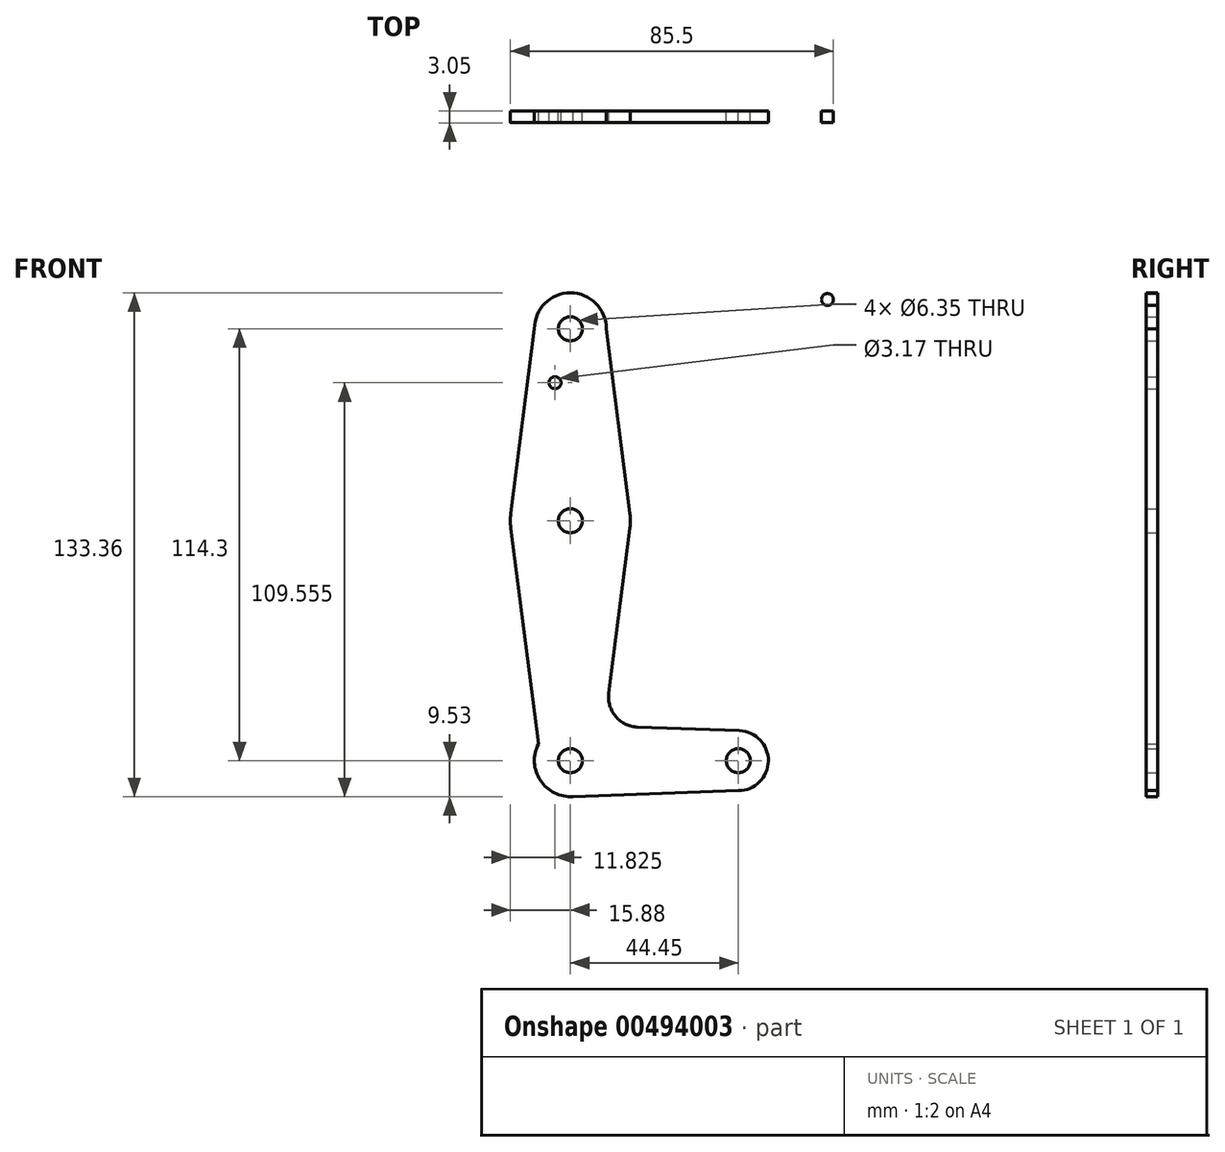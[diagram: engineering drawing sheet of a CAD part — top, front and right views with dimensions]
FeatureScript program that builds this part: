
annotation { "Feature Type Name" : "Feature", "Feature Type Description" : "" }
export const myFeature = defineFeature(function(context is Context, id is Id, definition is map)
    precondition{}
    {
        {
            var Q0;
            Q0=qCreatedBy(makeId("Front.planeOp"),FACE);
            var sketch = newSketch(context, id + "F0", { "sketchPlane" : qUnion([Q0])});
            skLineSegment(sketch, "E0", {"start": v(0, 0) * mm, "end": v(0, 114.3) * mm, "construction": true});
            skLineSegment(sketch, "E1", {"start": v(0, 0) * mm, "end": v(44.45, 0) * mm, "construction": true});
            skCircle(sketch, "E2", {"center": v(0, 114.3) * mm, "radius": 9.53 * mm});
            skCircle(sketch, "E3", {"center": v(0, 0) * mm, "radius": 9.53 * mm});
            skCircle(sketch, "E4", {"center": v(0, 63.5) * mm, "radius": 15.88 * mm});
            skLineSegment(sketch, "E5", {"start": v(9.53, 114.3) * mm, "end": v(15.75, 65.5) * mm});
            skLineSegment(sketch, "E6", {"start": v(-9.53, 114.3) * mm, "end": v(-15.75, 65.5) * mm});
            skLineSegment(sketch, "E7", {"start": v(15.75, 61.5) * mm, "end": v(10.18, 17.84) * mm});
            skLineSegment(sketch, "E8", {"start": v(-15.75, 61.5) * mm, "end": v(-8.46, 4.37) * mm});
            skCircle(sketch, "E9", {"center": v(44.45, 0) * mm, "radius": 7.94 * mm});
            skLineSegment(sketch, "E10", {"start": v(17.78, 8.9) * mm, "end": v(44.73, 7.93) * mm});
            skLineSegment(sketch, "E11", {"start": v(0, -9.53) * mm, "end": v(44.45, -7.94) * mm});
            skCircle(sketch, "E12", {"center": v(68.04, 122.06) * mm, "radius": 1.59 * mm});
            skCircle(sketch, "E13", {"center": v(44.45, 0) * mm, "radius": 3.18 * mm});
            skCircle(sketch, "E14", {"center": v(0, 0) * mm, "radius": 3.18 * mm});
            skCircle(sketch, "E15", {"center": v(0, 63.5) * mm, "radius": 3.18 * mm});
            skCircle(sketch, "E16", {"center": v(0, 114.3) * mm, "radius": 3.18 * mm});
            skCircle(sketch, "E17", {"center": v(-4.05, 100.03) * mm, "radius": 1.59 * mm});
            skPoint(sketch, "E18.newPointA", {"position": v(8.46, 4.37) * mm});
            skArc(sketch, "E18.filletArc", {"start": v(10.18, 17.84) * mm, "mid": v(12, 11.69) * mm, "end": v(17.78, 8.9) * mm});
            skSolve(sketch);
        }
        {
            var Q0;
            Q0 = qSketchRegion(id + "F0", true);
            extrude(context, id + "F1", {"entities" : qUnion([Q0]), "depth" : 3.05 * mm});
        }
    });
